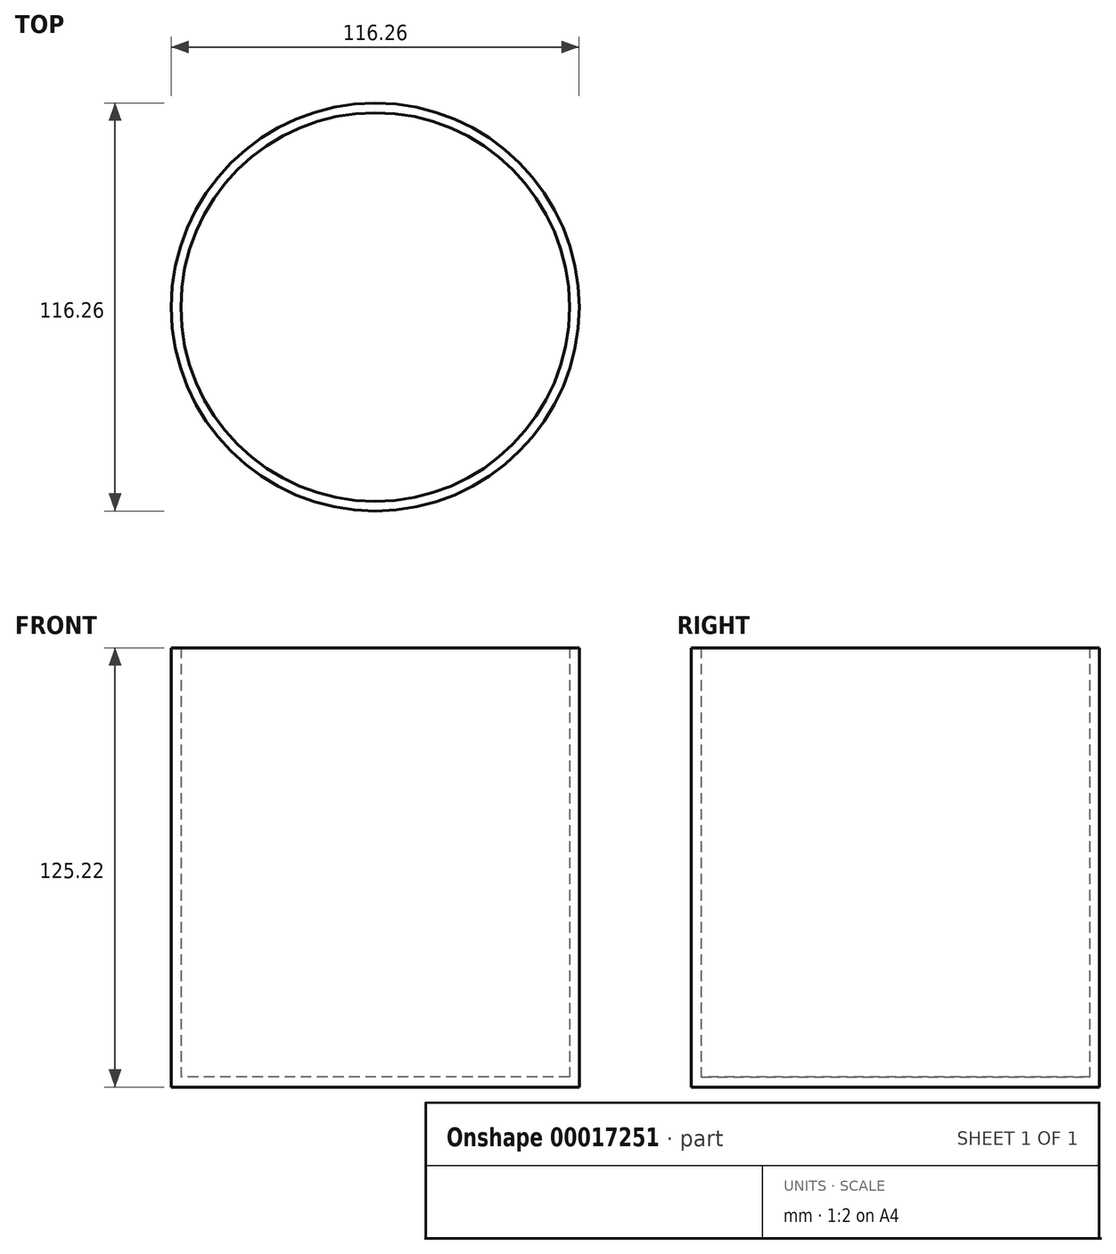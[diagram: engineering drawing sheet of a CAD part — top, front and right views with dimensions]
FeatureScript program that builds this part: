
annotation { "Feature Type Name" : "Feature", "Feature Type Description" : "" }
export const myFeature = defineFeature(function(context is Context, id is Id, definition is map)
    precondition{}
    {
        {
            var Q0;
            Q0=qCreatedBy(makeId("Top.planeOp"),FACE);
            var sketch = newSketch(context, id + "F0", { "sketchPlane" : qUnion([Q0])});
            skCircle(sketch, "E0", {"center": v(0, 0) * mm, "radius": 55.4 * mm});
            skCircle(sketch, "E1", {"center": v(0, 0) * mm, "radius": 58.13 * mm});
            skSolve(sketch);
        }
        {
            var Q0;
            Q0=makeQuery(id+"F0.imprint","IMPRINT",FACE,{"disambiguationData":[TD([[makeQuery(id+"F0.imprint","IMPRINT",EDGE,{"derivedFrom":sQuery(id+"F0.wireOp",EDGE,"E0")}),-1.0]])]});
            extrude(context, id + "F1", {"entities" : qUnion([Q0]), "depth" : 125.22 * mm});
        }
        {
            var Q0;
            Q0=makeQuery(id+"F0.imprint","IMPRINT",FACE,{"disambiguationData":[TD([[makeQuery(id+"F0.imprint","IMPRINT",EDGE,{"derivedFrom":sQuery(id+"F0.wireOp",EDGE,"E0")}),1.0]])]});
            extrude(context, id + "F2", {"entities" : qUnion([Q0]), "operationType" : NewBodyOperationType.ADD, "depth" : 2.84 * mm});
        }
        {
            var Q0;
            Q0=qCreatedBy(makeId("Right.planeOp"),FACE);
            var sketch = newSketch(context, id + "F3", { "sketchPlane" : qUnion([Q0])});
            skFitSpline(sketch, "E2", {"points": [v(57.76, 90.46) * mm, v(91.42, 53.4) * mm, v(57.3, 20.42) * mm], "startDerivative": vector(100.77, -74.75) * mm, "endDerivative": vector(-102.6, -65.3) * mm});
            skSolve(sketch);
        }
        {
            var Q0;
            Q0=sQuery(id+"F3.wireOp",EDGE,"E2");
            extrude(context, id + "F4", {"bodyType" : ToolBodyType.SURFACE, "surfaceEntities" : qUnion([Q0]), "oppositeDirection" : true, "depth" : 13.43 * mm});
        }
    });
